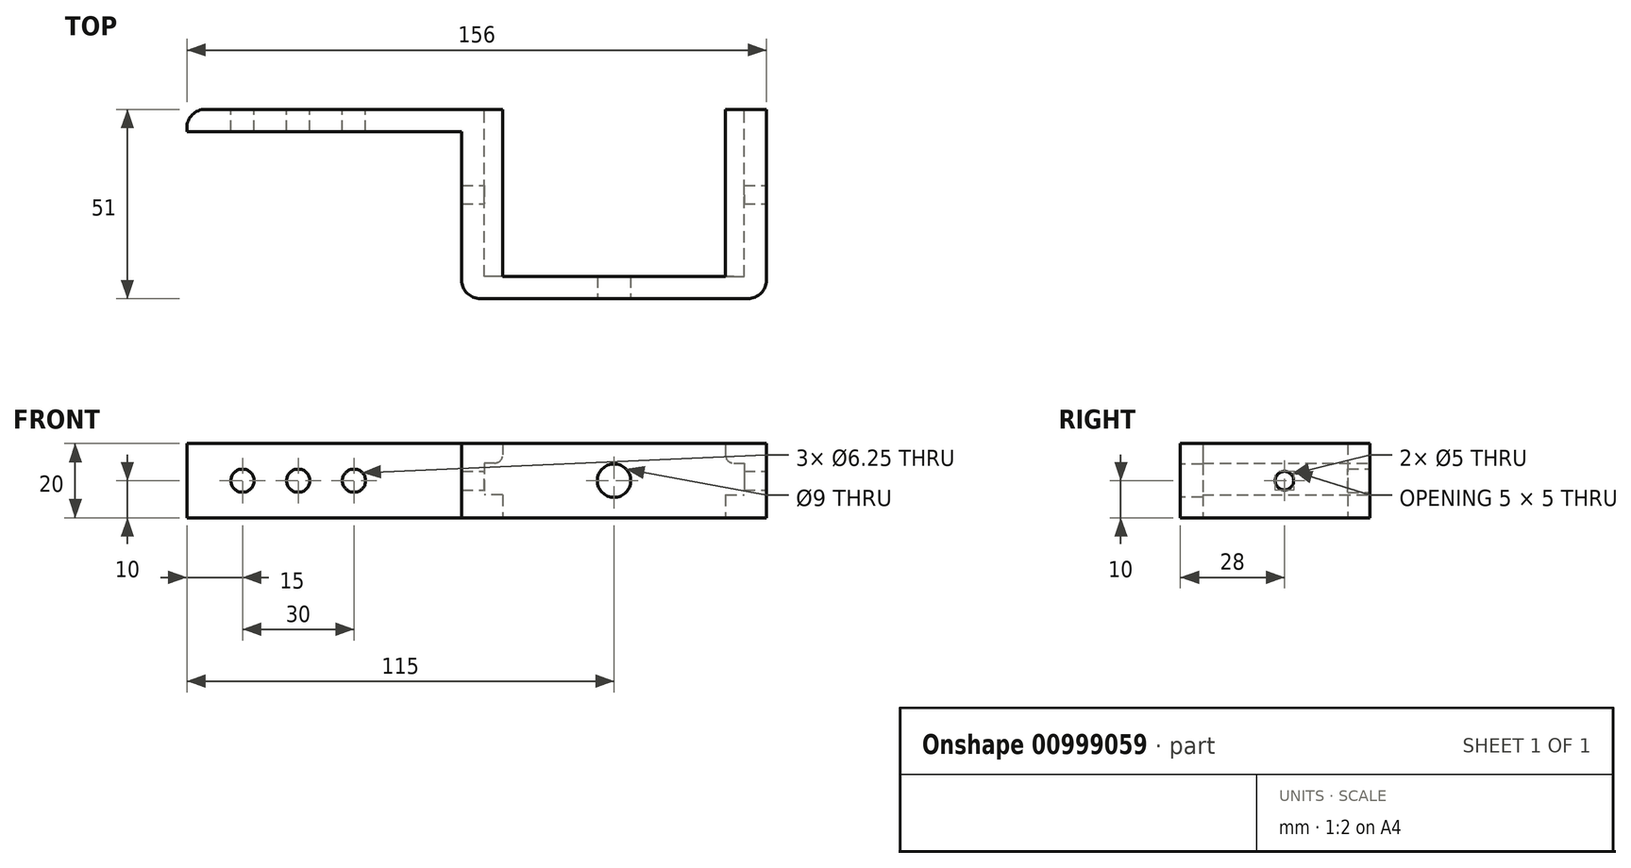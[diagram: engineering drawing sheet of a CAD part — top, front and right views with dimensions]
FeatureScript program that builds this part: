
annotation { "Feature Type Name" : "Feature", "Feature Type Description" : "" }
export const myFeature = defineFeature(function(context is Context, id is Id, definition is map)
    precondition{}
    {
        {
            var Q0;
            Q0=qCreatedBy(makeId("Top.planeOp"),FACE);
            var sketch = newSketch(context, id + "F0", { "sketchPlane" : qUnion([Q0])});
            skLineSegment(sketch, "E0", {"start": v(0, 0) * mm, "end": v(80, 0) * mm});
            skLineSegment(sketch, "E1", {"start": v(80, 0) * mm, "end": v(80, -45) * mm});
            skLineSegment(sketch, "E2", {"start": v(80, -45) * mm, "end": v(150, -45) * mm});
            skLineSegment(sketch, "E3", {"start": v(150, -45) * mm, "end": v(150, 0) * mm});
            skLineSegment(sketch, "E4", {"start": v(150, 0) * mm, "end": v(156, 0) * mm});
            skLineSegment(sketch, "E5", {"start": v(156, 0) * mm, "end": v(156, -51) * mm});
            skLineSegment(sketch, "E6", {"start": v(156, -51) * mm, "end": v(74, -51) * mm});
            skLineSegment(sketch, "E7", {"start": v(74, -51) * mm, "end": v(74, -6) * mm});
            skLineSegment(sketch, "E8", {"start": v(74, -6) * mm, "end": v(0, -6) * mm});
            skLineSegment(sketch, "E9", {"start": v(0, -6) * mm, "end": v(0, 0) * mm});
            skSolve(sketch);
        }
        {
            var Q0;
            Q0 = qSketchRegion(id + "F0", true);
            extrude(context, id + "F1", {"entities" : qUnion([Q0]), "depth" : 20 * mm, "offsetDistance" : 25 * mm});
        }
        {
            var Q0;
            Q0=makeQuery(id+"F1.opExtrude","SWEPT_FACE",FACE,{"disambiguationData":[OSD([sQuery(id+"F0.wireOp",EDGE,"E0")])]});
            var sketch = newSketch(context, id + "F2", { "sketchPlane" : qUnion([Q0])});
            skPoint(sketch, "E10", {"position": v(-15, 10) * mm});
            skPoint(sketch, "E11", {"position": v(-30, 10) * mm});
            skPoint(sketch, "E12", {"position": v(-45, 10) * mm});
            skSolve(sketch);
        }
        {
            var Q0;
            Q0=sQuery(id+"F2.wireOp",VERTEX,"E12");
            var Q1;
            Q1=sQuery(id+"F2.wireOp",VERTEX,"E11");
            var Q2;
            Q2=sQuery(id+"F2.wireOp",VERTEX,"E10");
            var Q3;
            Q3=makeQuery(id+"F1.opExtrude","SWEPT_BODY",BODY,{"disambiguationData":[OSD([sQuery(id+"F0.wireOp",EDGE,"E0"),sQuery(id+"F0.wireOp",EDGE,"E1"),sQuery(id+"F0.wireOp",EDGE,"E2"),sQuery(id+"F0.wireOp",EDGE,"E3"),sQuery(id+"F0.wireOp",EDGE,"E4"),sQuery(id+"F0.wireOp",EDGE,"E5"),sQuery(id+"F0.wireOp",EDGE,"E6"),sQuery(id+"F0.wireOp",EDGE,"E7"),sQuery(id+"F0.wireOp",EDGE,"E8"),sQuery(id+"F0.wireOp",EDGE,"E9")])]});
            hole(context, id + "F3", {"style" : HoleStyle.SIMPLE, "endStyle" : HoleEndStyle.THROUGH, "standardTappedOrClearance" : lookupTablePath({ "standard" : "ANSI", "size" : "D (0.25)", "type" : "Drilled" }), "standardBlindInLast" : lookupTablePath({ "standard" : "ANSI", "size" : "D (0.25)", "type" : "Drilled" }), "holeDiameter" : 6.25 * mm, "majorDiameter" : 5 * mm, "isTappedThrough" : true, "tappedDepth" : 12 * mm, "tapClearance" : 3, "locations" : qUnion([Q0, Q1, Q2]), "scope" : qUnion([Q3])});
        }
        {
            var Q0;
            Q0=makeQuery(id+"F1.opExtrude","SWEPT_FACE",FACE,{"disambiguationData":[OSD([sQuery(id+"F0.wireOp",EDGE,"E1")])]});
            var sketch = newSketch(context, id + "F4", { "sketchPlane" : qUnion([Q0])});
            skLineSegment(sketch, "E13", {"start": v(-45, 6.15) * mm, "end": v(0, 6.15) * mm});
            skLineSegment(sketch, "E14", {"start": v(-45, 14.75) * mm, "end": v(0, 14.75) * mm});
            skSolve(sketch);
        }
        {
            var Q0;
            Q0=makeQuery(id+"F1.opExtrude","SWEPT_FACE",FACE,{"disambiguationData":[OSD([sQuery(id+"F0.wireOp",EDGE,"E3")])]});
            var sketch = newSketch(context, id + "F5", { "sketchPlane" : qUnion([Q0])});
            skLineSegment(sketch, "E15", {"start": v(0, 14.75) * mm, "end": v(45, 14.75) * mm});
            skLineSegment(sketch, "E16", {"start": v(45, 6.15) * mm, "end": v(0, 6.15) * mm});
            skSolve(sketch);
        }
        {
            var Q0;
            {var subQ0=sQuery(id+"F5.wireOp",EDGE,"E15");Q0=makeQuery(id+"F5.imprint","IMPRINT",FACE,{"disambiguationData":[TD([[makeQuery(id+"F5.imprint","IMPRINT",EDGE,{"derivedFrom":subQ0}),1.0]])]});}
            var Q1;
            {var subQ0=sQuery(id+"F5.wireOp",EDGE,"E16");Q1=makeQuery(id+"F5.imprint","IMPRINT",FACE,{"disambiguationData":[TD([[makeQuery(id+"F5.imprint","IMPRINT",EDGE,{"derivedFrom":subQ0}),1.0]])]});}
            extrude(context, id + "F6", {"entities" : qUnion([Q0, Q1]), "operationType" : NewBodyOperationType.ADD, "depth" : 5 * mm, "offsetDistance" : 25 * mm});
        }
        {
            var Q0;
            {var subQ0=sQuery(id+"F4.wireOp",EDGE,"E14");Q0=makeQuery(id+"F4.imprint","IMPRINT",FACE,{"disambiguationData":[TD([[makeQuery(id+"F4.imprint","IMPRINT",EDGE,{"derivedFrom":subQ0}),1.0]])]});}
            var Q1;
            {var subQ0=sQuery(id+"F4.wireOp",EDGE,"E13");Q1=makeQuery(id+"F4.imprint","IMPRINT",FACE,{"disambiguationData":[TD([[makeQuery(id+"F4.imprint","IMPRINT",EDGE,{"derivedFrom":subQ0}),-1.0]])]});}
            extrude(context, id + "F7", {"entities" : qUnion([Q0, Q1]), "operationType" : NewBodyOperationType.ADD, "depth" : 5 * mm, "offsetDistance" : 25 * mm});
        }
        {
            var Q0;
            Q0=makeQuery(id+"F1.opExtrude","SWEPT_EDGE",EDGE,{"disambiguationData":[OSD([sQuery(id+"F0.wireOp",EDGE,"E6"),sQuery(id+"F0.wireOp",EDGE,"E7")])]});
            var Q1;
            Q1=makeQuery(id+"F1.opExtrude","SWEPT_EDGE",EDGE,{"disambiguationData":[OSD([sQuery(id+"F0.wireOp",EDGE,"E5"),sQuery(id+"F0.wireOp",EDGE,"E6")])]});
            var Q2;
            Q2=makeQuery(id+"F1.opExtrude","SWEPT_EDGE",EDGE,{"disambiguationData":[OSD([sQuery(id+"F0.wireOp",EDGE,"E0"),sQuery(id+"F0.wireOp",EDGE,"E9")])]});
            fillet(context, id + "F8", {"entities" : qUnion([Q0, Q1, Q2]), "radius" : 5 * mm, "tangentPropagation" : true, "allowEdgeOverflow" : false});
        }
        {
            var Q0;
            Q0=makeQuery(id+"F7.opExtrude","CAP_EDGE",EDGE,{"disambiguationData":[OSD([sQuery(id+"F4.wireOp",EDGE,"E14")])],"isStart":false});
            var Q1;
            Q1=makeQuery(id+"F6.opExtrude","CAP_EDGE",EDGE,{"disambiguationData":[OSD([sQuery(id+"F5.wireOp",EDGE,"E15")])],"isStart":false});
            fillet(context, id + "F9", {"entities" : qUnion([Q0, Q1]), "radius" : 2.2 * mm, "tangentPropagation" : true, "allowEdgeOverflow" : false});
        }
        {
            var Q0;
            Q0=makeQuery(id+"F1.opExtrude","SWEPT_FACE",FACE,{"disambiguationData":[OSD([sQuery(id+"F0.wireOp",EDGE,"E6")])]});
            var sketch = newSketch(context, id + "F10", { "sketchPlane" : qUnion([Q0])});
            skPoint(sketch, "E17", {"position": v(115, 10) * mm});
            skSolve(sketch);
        }
        {
            var Q0;
            Q0=sQuery(id+"F10.wireOp",VERTEX,"E17");
            var Q1;
            Q1=makeQuery(id+"F1.opExtrude","SWEPT_BODY",BODY,{"disambiguationData":[OSD([sQuery(id+"F0.wireOp",EDGE,"E0"),sQuery(id+"F0.wireOp",EDGE,"E1"),sQuery(id+"F0.wireOp",EDGE,"E2"),sQuery(id+"F0.wireOp",EDGE,"E3"),sQuery(id+"F0.wireOp",EDGE,"E4"),sQuery(id+"F0.wireOp",EDGE,"E5"),sQuery(id+"F0.wireOp",EDGE,"E6"),sQuery(id+"F0.wireOp",EDGE,"E7"),sQuery(id+"F0.wireOp",EDGE,"E8"),sQuery(id+"F0.wireOp",EDGE,"E9")])]});
            hole(context, id + "F11", {"style" : HoleStyle.SIMPLE, "endStyle" : HoleEndStyle.THROUGH, "standardTappedOrClearance" : lookupTablePath({ "fit" : "Normal", "standard" : "ISO", "size" : "9", "type" : "Drilled" }), "standardBlindInLast" : lookupTablePath({ "standard" : "ISO", "size" : "9", "type" : "Drilled" }), "holeDiameter" : 9 * mm, "majorDiameter" : 5 * mm, "isTappedThrough" : true, "tappedDepth" : 12 * mm, "tapClearance" : 3, "locations" : qUnion([Q0]), "scope" : qUnion([Q1])});
        }
        {
            var Q0;
            Q0=makeQuery(id+"F1.opExtrude","SWEPT_FACE",FACE,{"disambiguationData":[OSD([sQuery(id+"F0.wireOp",EDGE,"E5")])]});
            var sketch = newSketch(context, id + "F12", { "sketchPlane" : qUnion([Q0])});
            skPoint(sketch, "E18", {"position": v(-23, 10) * mm});
            skSolve(sketch);
        }
        {
            var Q0;
            Q0=sQuery(id+"F12.wireOp",VERTEX,"E18");
            var Q1;
            Q1=makeQuery(id+"F1.opExtrude","SWEPT_BODY",BODY,{"disambiguationData":[OSD([sQuery(id+"F0.wireOp",EDGE,"E0"),sQuery(id+"F0.wireOp",EDGE,"E1"),sQuery(id+"F0.wireOp",EDGE,"E2"),sQuery(id+"F0.wireOp",EDGE,"E3"),sQuery(id+"F0.wireOp",EDGE,"E4"),sQuery(id+"F0.wireOp",EDGE,"E5"),sQuery(id+"F0.wireOp",EDGE,"E6"),sQuery(id+"F0.wireOp",EDGE,"E7"),sQuery(id+"F0.wireOp",EDGE,"E8"),sQuery(id+"F0.wireOp",EDGE,"E9")])]});
            hole(context, id + "F13", {"style" : HoleStyle.SIMPLE, "endStyle" : HoleEndStyle.THROUGH, "holeDiameter" : 5 * mm, "majorDiameter" : 5 * mm, "isTappedThrough" : true, "tappedDepth" : 12 * mm, "tapClearance" : 3, "locations" : qUnion([Q0]), "scope" : qUnion([Q1])});
        }
    });
